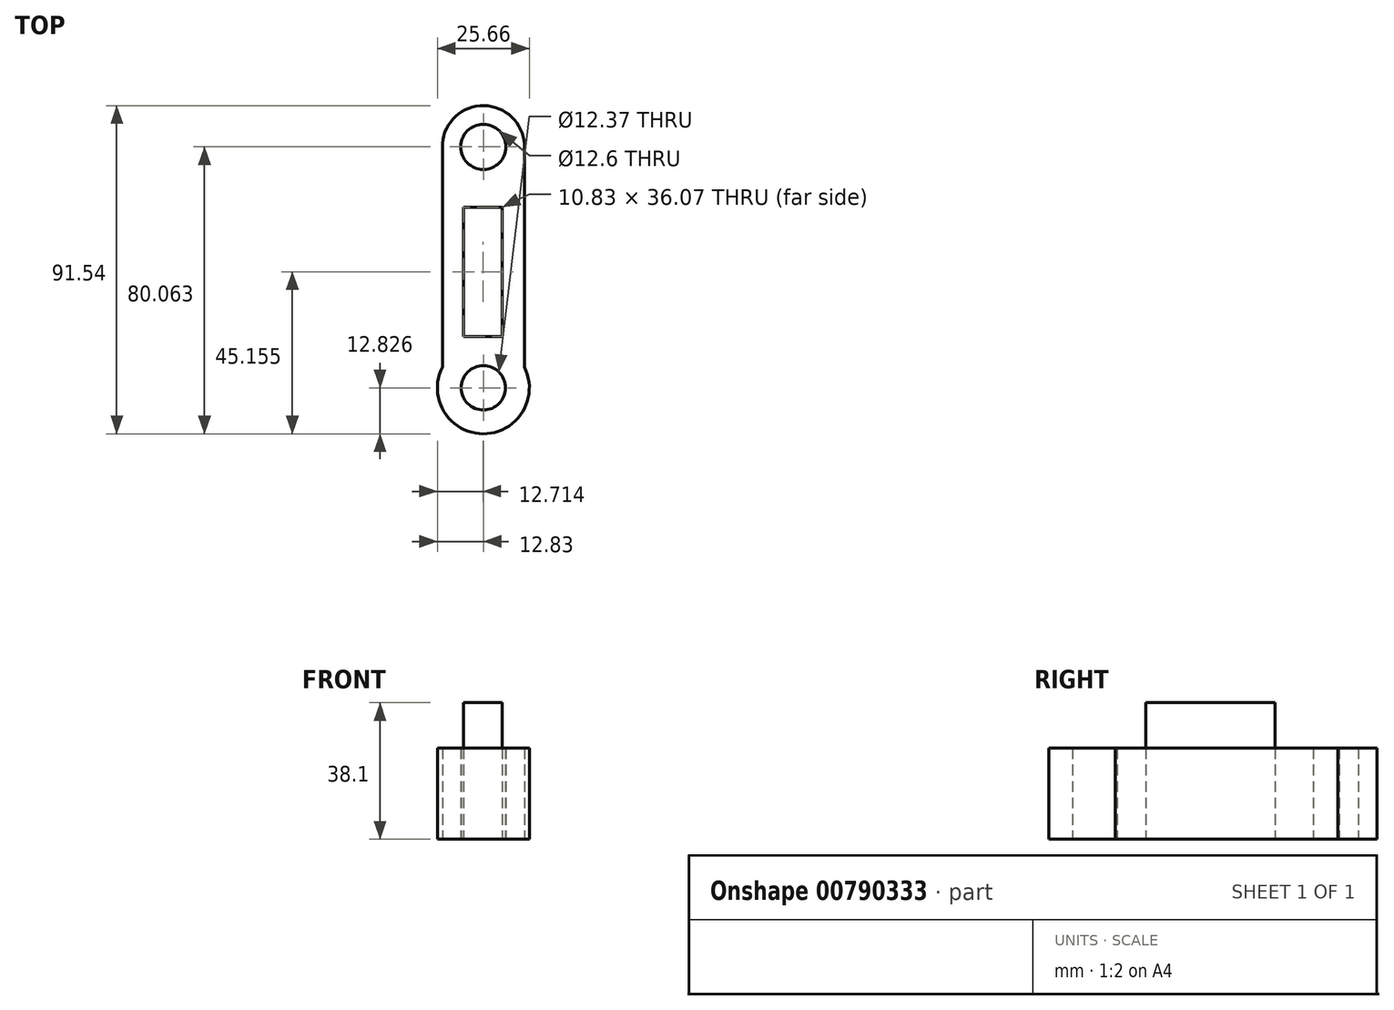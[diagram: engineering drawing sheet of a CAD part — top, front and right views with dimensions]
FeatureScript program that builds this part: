
annotation { "Feature Type Name" : "Feature", "Feature Type Description" : "" }
export const myFeature = defineFeature(function(context is Context, id is Id, definition is map)
    precondition{}
    {
        {
            var Q0;
            Q0=qCreatedBy(makeId("Top.planeOp"),FACE);
            var sketch = newSketch(context, id + "F0", { "sketchPlane" : qUnion([Q0])});
            skArc(sketch, "E0", {"start": v(11.45, 46.21) * mm, "mid": v(-0.15, 58.34) * mm, "end": v(-11.43, 45.9) * mm});
            skLineSegment(sketch, "E1", {"start": v(-11.43, 47.84) * mm, "end": v(-11.43, -14.58) * mm});
            skLineSegment(sketch, "E2", {"start": v(11.45, 47.54) * mm, "end": v(11.45, -14.58) * mm});
            skArc(sketch, "E3", {"start": v(-11.43, -14.54) * mm, "mid": v(-0.02, -33.2) * mm, "end": v(11.45, -14.58) * mm});
            skLineSegment(sketch, "E4", {"start": v(0.15, 58.34) * mm, "end": v(0, 46.87) * mm});
            skPoint(sketch, "E4.startSnap0", {"position": v(-0.15, 58.34) * mm});
            skLineSegment(sketch, "E5", {"start": v(0, 46.87) * mm, "end": v(0, -33.2) * mm});
            skCircle(sketch, "E6", {"center": v(0, -20.36) * mm, "radius": 6.19 * mm});
            skCircle(sketch, "E7", {"center": v(0, 46.87) * mm, "radius": 6.3 * mm});
            skLineSegment(sketch, "E8.bottom", {"start": v(5.3, -6.07) * mm, "end": v(-5.53, -6.07) * mm});
            skLineSegment(sketch, "E8.top", {"start": v(5.3, 30) * mm, "end": v(-5.53, 30) * mm});
            skLineSegment(sketch, "E8.left", {"start": v(5.3, -6.07) * mm, "end": v(5.3, 30) * mm});
            skLineSegment(sketch, "E8.right", {"start": v(-5.53, -6.07) * mm, "end": v(-5.53, 30) * mm});
            skSolve(sketch);
        }
        {
            var Q0;
            {var subQ16=sQuery(id+"F0.wireOp",EDGE,"E8.left");Q0=makeQuery(id+"F0.imprint","IMPRINT",FACE,{"disambiguationData":[TD([[makeQuery(id+"F0.imprint","IMPRINT",EDGE,{"derivedFrom":subQ16}),-1.0]])]});}
            var Q1;
            {var subQ16=sQuery(id+"F0.wireOp",EDGE,"E8.right");Q1=makeQuery(id+"F0.imprint","IMPRINT",FACE,{"disambiguationData":[TD([[makeQuery(id+"F0.imprint","IMPRINT",EDGE,{"derivedFrom":subQ16}),1.0]])]});}
            extrude(context, id + "F1", {"entities" : qUnion([Q0, Q1]), "depth" : 25.4 * mm, "offsetDistance" : 25.4 * mm});
        }
        {
            var Q0;
            Q0=makeQuery(id+"F1.opExtrude","CAP_FACE",FACE,{"disambiguationData":[OSD([sQuery(id+"F0.wireOp",EDGE,"E0"),sQuery(id+"F0.wireOp",EDGE,"E1"),sQuery(id+"F0.wireOp",EDGE,"E2"),sQuery(id+"F0.wireOp",EDGE,"E3"),sQuery(id+"F0.wireOp",EDGE,"E6"),sQuery(id+"F0.wireOp",EDGE,"E7"),sQuery(id+"F0.wireOp",EDGE,"E8.bottom"),sQuery(id+"F0.wireOp",EDGE,"E8.top"),sQuery(id+"F0.wireOp",EDGE,"E8.left"),sQuery(id+"F0.wireOp",EDGE,"E8.right")])],"isStart":false});
            var sketch = newSketch(context, id + "F2", { "sketchPlane" : qUnion([Q0])});
            skLineSegment(sketch, "E9.bottom", {"start": v(-5.53, -6.07) * mm, "end": v(5.3, -6.07) * mm});
            skLineSegment(sketch, "E9.top", {"start": v(-5.53, 30) * mm, "end": v(5.3, 30) * mm});
            skLineSegment(sketch, "E9.left", {"start": v(-5.53, -6.07) * mm, "end": v(-5.53, 30) * mm});
            skLineSegment(sketch, "E9.right", {"start": v(5.3, -6.07) * mm, "end": v(5.3, 30) * mm});
            skSolve(sketch);
        }
        {
            var Q0;
            Q0=qSketchRegion(id+"F2",true);
            extrude(context, id + "F3", {"entities" : qUnion([Q0]), "depth" : 12.7 * mm, "offsetDistance" : 25.4 * mm});
        }
    });
